# Revit family: Faucet-Lavatory-KOHLER-ACCLIV-K-33063K_1
name_source: partatom
category: Plumbing Fixtures
units: mm (PartAtom-declared; Revit-internal decimal feet)

## family parameters
Cut with Voids When Loaded = No
Host = Face
OmniClass Number = 23.31.11.00
OmniClass Title = Faucets
Part Type = Normal
Room Calculation Point = No
Round Connector Dimension = Use Diameter
Shared = No

## types (4) — shared parameters
ADA Compliant = No
Assembly Code = D2010
CW Connection = Yes
Cold Water Inlet = Cold Water Inlet
Date Modified = 11/21/2022
Default Elevation = 36"
Description = Tall Single Control Lavatory Faucet
Drain Included = Yes
Faucet Hole Spacing = 0"
Flow Rate = 2 GPM
HW Connection = Yes
Handle Clearance = 3 15/16"
Height = 9 7/16"
Hot Water Inlet = Hot Water Inlet
Length = 5 9/16"
Manufacturer = Kohler Co.
Master Format 2014 = 22 41 39
Master Format 2014 Name = Residential Faucets, Supplies, and Trim
Material = Premium Metal Construction
Pressure = 45.00 psi
Product Documentation Link = https://resources.kohler.com
Product Name = ACCLIV
Spout Reach = 5 9/16"
URL = https://www.kohlerasiapacific.com
Vent Connection = No
Waste Connection = No
Waste Water Outlet = Waste Water Outlet
WaterSense Certified = No
Width = 2"

## per-type parameters (varying)
| type | Finish | Model | Product Page URL | Type |
| AF-Vibrant French Gold | Kohler-Metal-AF-Vibrant_French_Gold | K-33063K-4-AF | https://www.kohlerasiapacific.com | 1 |
| BL-Matte Black | Kohler-Metal-BL-Matte_Black | K-33063K-4-BL |  | 2 |
| BN-Vibrant Brushed Nickel | Kohler-Metal-BN-Vibrant_Brushed_Nickel | K-33063K-4-BN | https://www.kohlerasiapacific.com | 3 |
| CP-Polished Chrome | Kohler-Metal-CP-Polished_Chrome | K-33063K-4-CP | https://www.kohlerasiapacific.com | 4 |

## geometry (parser evidence)
native form markers: Sweep x4
no freeform markers — native parametric forms only
